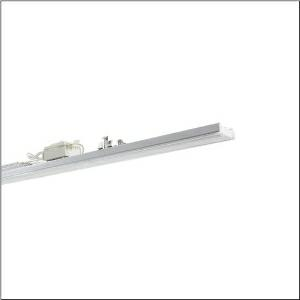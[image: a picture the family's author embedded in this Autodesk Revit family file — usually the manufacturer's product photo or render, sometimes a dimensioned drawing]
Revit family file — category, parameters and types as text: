
# Revit family: licross_r__11_recessed_mo_51tl12dne9xg_a7fb
name_source: partatom
category: Lighting Fixtures
units: mm (PartAtom-declared; Revit-internal decimal feet)

## family parameters
Cut with Voids When Loaded = No
Host = Face
Light Source = No
Part Type = Normal
Room Calculation Point = No
Round Connector Dimension = Use Diameter
Shared = No

## types (1)
- --- (1 x LED, 9450 lm, 56.2 W, 5000K)
    Apparent Load = 56 VA
    CIE Flux Codes = 67 92 99 100 100
    Color Rendering = 90
    Color Temperature = 5000K
    Default Elevation = 1800 mm
    Description = Licross® 11 Recessed MO, luminaire insert, of sheet steel, coil coated, white, length: 1.500mm, width: 66mm, height: 67mm, LED rated luminous flux: 9.450lm, light colour: 950, control gear: DALI 2, with plug, 5-pole, with phase selection, mains connection: 220..240V, AC, 50/60Hz, rated input power: 56W, internal wiring halogen-free, primary optical cover: cover, of PMMA, light emission: direct distribution, primary light characteristic: symmetric, protection rating (complete): IP40, insulation class (complete): insulation class I (protective earthing), certification: CE, ENEC, VDE, UKCA, protection symbol: D if used in an environment without relevant dust loads with corresponding accessories, impact resistance: IK06, permissible ambient temperature for indoor applications: -25..+35°C, corresponds to IFS (International Featured Standards) requirements for safety and quality in the food industry, reducing of maximum allowable ambient temperature of 5°C with ceiling mounting, LABS conformity tested according to VDMA 24364:2018-05, packaging unit: 1 piece
    Height = 58 mm
    Lamp = 1 x LED
    Lamp Light Flux = 9450 lm
    Lamp Power = 56.2 W
    Lamp count = 1
    Length = 1500 mm
    Luminous efficacy = 168 lm/W
    Manufacturer = Siteco
    ModVariant = No
    Model = 51TL12DNE9XG
    Mounting Place = Ceiling
    Mounting Type = Pendant
    Number of Poles = 1
    OnlyDefault = Yes
    Power Factor = 1
    Product Name = Licross® 11 Recessed MO
    Product group = luminaire insert | ceiling pendant
    ProductGroupID = 902
    Protection Class = Protection class I
    Protection Degree = IP 40
    RLX_Detail_Level = 1
    RLX_Emergency_Light_Flux = 0 lm
    RLX_Emergency_Type = 0
    RLX_Emergency_Type_DB = No
    RlxData = <blob elided: 24485 chars, md5=386820a0>
    Socket = socket
    Standby Power = 0 W
    System Light Flux = 9450 lm
    System Power = 56 W
    Type Comments = factory setting: luminous flux: 100 % | dim-lin: 254 | 378 mA
    Type Image = l_1296930.jpg
    URL = http://relux.com
    VarID = @adj_069595
    Voltage = 0 V
    Weight = 0.00 kg
    Width = 66 mm

## geometry (parser evidence)
native form markers: Blend x4, Sweep x10
no freeform markers — native parametric forms only
